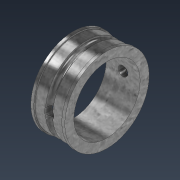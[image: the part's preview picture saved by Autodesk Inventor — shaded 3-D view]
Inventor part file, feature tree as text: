
AUTODESK INVENTOR PART (.ipt)
format: ipt  version: 2022 (Build 260153000, 153)  size: 170,496 bytes
history: native  units: mm
features: sketch x2, revolve x1, extrude x1
ambient origin geometry x8: Origin, YZ Plane, XZ Plane, XY Plane, X Axis, Y Axis, Z Axis, Center Point
bodies: Solid1 (feature_tree)
feature tree (4):
  revolve  "Revolution1"  [1 undecoded]
  extrude  "Extrusion1"  Depth=28.172mm
  sketch  "Sketch1"  dims[d0=100.0mm d1=3.0mm]
  sketch  "Sketch2"  dims[d3=55.0mm d4=28.172mm d5=90.0deg d6=8.0mm d7=0.0mm d8=0.0mm d9=2.5mm d10=1.0mm d11=70.0mm]
note: 1 required parameter value undecoded (feature->parameter linkage not recoverable at this tier; creation-order binding heuristic only, values carry confidence <= 0.55)
